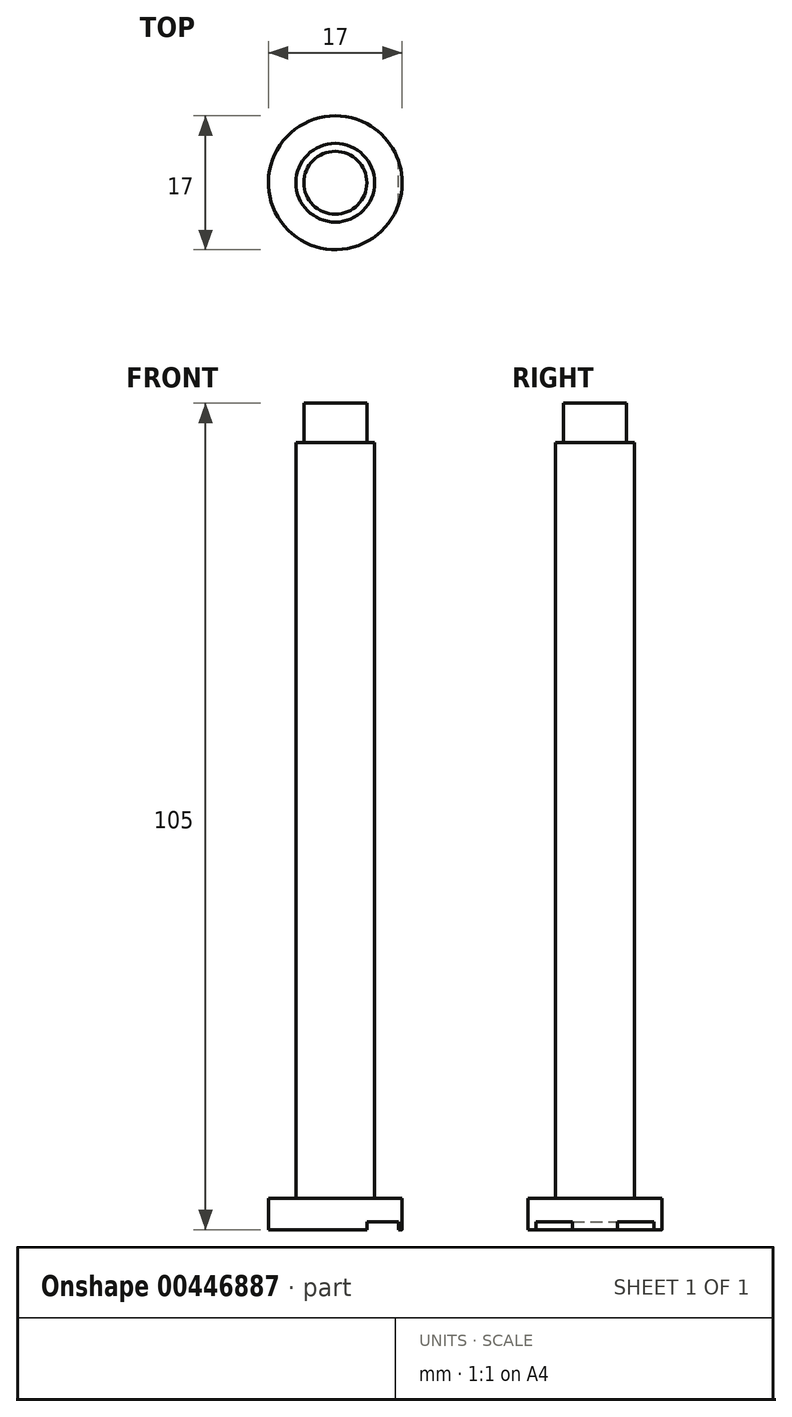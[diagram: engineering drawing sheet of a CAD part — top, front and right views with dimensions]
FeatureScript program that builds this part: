
annotation { "Feature Type Name" : "Feature", "Feature Type Description" : "" }
export const myFeature = defineFeature(function(context is Context, id is Id, definition is map)
    precondition{}
    {
        {
            var Q0;
            Q0=qCreatedBy(makeId("Top.planeOp"),FACE);
            var sketch = newSketch(context, id + "F0", { "sketchPlane" : qUnion([Q0])});
            skCircle(sketch, "E0", {"center": v(0, 0) * mm, "radius": 8.5 * mm});
            skSolve(sketch);
        }
        {
            var Q0;
            Q0=qSketchRegion(id+"F0",true);
            extrude(context, id + "F1", {"entities" : qUnion([Q0]), "depth" : 4 * mm});
        }
        {
            var Q0;
            Q0=qCreatedBy(makeId("Top.planeOp"),FACE);
            var sketch = newSketch(context, id + "F2", { "sketchPlane" : qUnion([Q0])});
            skCircle(sketch, "E1", {"center": v(0, 0) * mm, "radius": 5 * mm});
            skSolve(sketch);
        }
        {
            var Q0;
            Q0=qSketchRegion(id+"F2",true);
            extrude(context, id + "F3", {"entities" : qUnion([Q0]), "operationType" : NewBodyOperationType.ADD, "depth" : 100 * mm});
        }
        {
            var Q0;
            Q0=qCreatedBy(makeId("Right.planeOp"),FACE);
            var sketch = newSketch(context, id + "F4", { "sketchPlane" : qUnion([Q0])});
            skLineSegment(sketch, "E2.bottom", {"start": v(0, 105) * mm, "end": v(4, 105) * mm});
            skLineSegment(sketch, "E2.top", {"start": v(0, 100) * mm, "end": v(4, 100) * mm});
            skLineSegment(sketch, "E2.left", {"start": v(0, 105) * mm, "end": v(0, 100) * mm});
            skLineSegment(sketch, "E2.right", {"start": v(4, 105) * mm, "end": v(4, 100) * mm});
            skSolve(sketch);
        }
        {
            var Q0;
            Q0=makeQuery(id+"F4.imprint","IMPRINT",FACE,{"disambiguationData":[TD([[makeQuery(id+"F4.imprint","IMPRINT",EDGE,{"derivedFrom":sQuery(id+"F4.wireOp",EDGE,"E2.bottom")}),-1.0]])]});
            var Q1;
            Q1=sQuery(id+"F4.wireOp",EDGE,"E2.left");
            revolve(context, id + "F5", {"operationType" : NewBodyOperationType.ADD, "entities" : qUnion([Q0]), "axis" : qUnion([Q1]), "revolveType" : RevolveType.FULL});
        }
        {
            var Q0;
            Q0=makeQuery(id+"F1.opExtrude","CAP_FACE",FACE,{"disambiguationData":[OSD([sQuery(id+"F0.wireOp",EDGE,"E0")])],"isStart":true});
            var sketch = newSketch(context, id + "F6", { "sketchPlane" : qUnion([Q0])});
            skLineSegment(sketch, "E3.bottom", {"start": v(4, 17.7) * mm, "end": v(8, 17.7) * mm});
            skLineSegment(sketch, "E3.top", {"start": v(4, -19.2) * mm, "end": v(8, -19.2) * mm});
            skLineSegment(sketch, "E3.left", {"start": v(4, 17.7) * mm, "end": v(4, -19.2) * mm});
            skLineSegment(sketch, "E3.right", {"start": v(8, 17.7) * mm, "end": v(8, -19.2) * mm});
            skSolve(sketch);
        }
        {
            var Q0;
            Q0=qSketchRegion(id+"F6",true);
            extrude(context, id + "F7", {"entities" : qUnion([Q0]), "operationType" : NewBodyOperationType.REMOVE, "oppositeDirection" : true, "depth" : 1 * mm});
        }
    });
